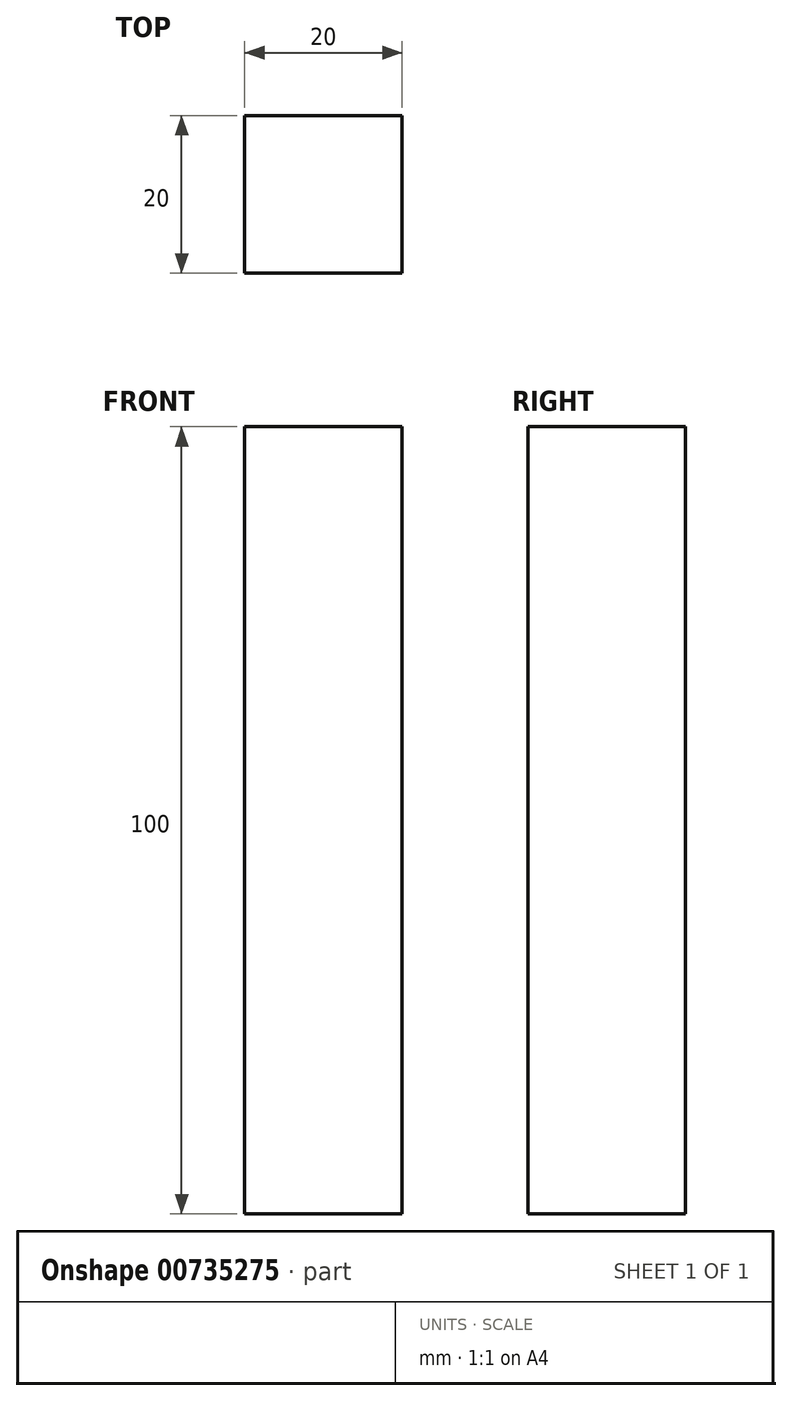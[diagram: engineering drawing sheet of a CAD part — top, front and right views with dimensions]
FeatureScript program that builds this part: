
annotation { "Feature Type Name" : "Feature", "Feature Type Description" : "" }
export const myFeature = defineFeature(function(context is Context, id is Id, definition is map)
    precondition{}
    {
        {
            var Q0;
            Q0=qCreatedBy(makeId("Top.planeOp"),FACE);
            var sketch = newSketch(context, id + "F0", { "sketchPlane" : qUnion([Q0])});
            skLineSegment(sketch, "E0.bottom", {"start": v(10, 10) * mm, "end": v(-10, 10) * mm});
            skLineSegment(sketch, "E0.top", {"start": v(10, -10) * mm, "end": v(-10, -10) * mm});
            skLineSegment(sketch, "E0.left", {"start": v(10, 10) * mm, "end": v(10, -10) * mm});
            skLineSegment(sketch, "E0.right", {"start": v(-10, 10) * mm, "end": v(-10, -10) * mm});
            skPoint(sketch, "E0.middle", {"position": v(0, 0) * mm});
            skSolve(sketch);
        }
        {
            var Q0;
            Q0=makeQuery(id+"F0.imprint","IMPRINT",FACE,{"disambiguationData":[TD([[makeQuery(id+"F0.imprint","IMPRINT",EDGE,{"derivedFrom":sQuery(id+"F0.wireOp",EDGE,"E0.bottom")}),1.0]])]});
            extrude(context, id + "F1", {"entities" : qUnion([Q0]), "depth" : 100 * mm, "offsetDistance" : 25 * mm});
        }
    });
